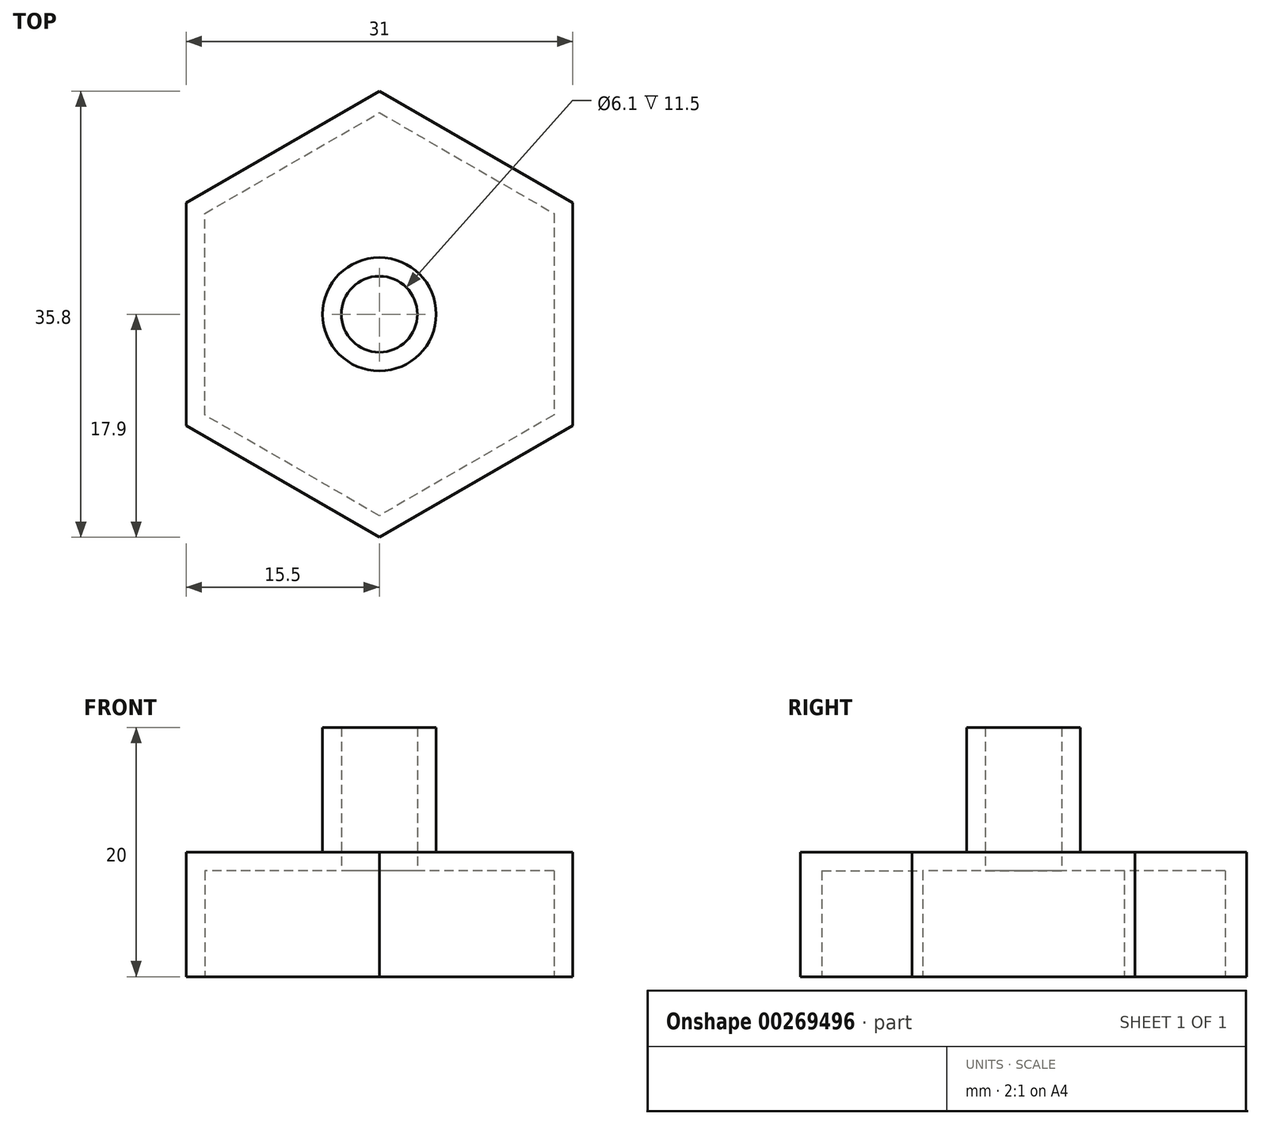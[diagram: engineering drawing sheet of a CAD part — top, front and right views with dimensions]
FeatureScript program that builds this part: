
annotation { "Feature Type Name" : "Feature", "Feature Type Description" : "" }
export const myFeature = defineFeature(function(context is Context, id is Id, definition is map)
    precondition{}
    {
        {
            var Q0;
            Q0=qCreatedBy(makeId("Top.planeOp"),FACE);
            var sketch = newSketch(context, id + "F0", { "sketchPlane" : qUnion([Q0])});
            skCircle(sketch, "E0.cCircle", {"center": v(0, 0) * mm, "radius": 17.9 * mm, "construction": true});
            skLineSegment(sketch, "E0.0", {"start": v(0, -17.9) * mm, "end": v(-15.5, -8.95) * mm});
            skLineSegment(sketch, "E0.1", {"start": v(-15.5, -8.95) * mm, "end": v(-15.5, 8.95) * mm});
            skLineSegment(sketch, "E0.2", {"start": v(-15.5, 8.95) * mm, "end": v(0, 17.9) * mm});
            skLineSegment(sketch, "E0.3", {"start": v(0, 17.9) * mm, "end": v(15.5, 8.95) * mm});
            skLineSegment(sketch, "E0.4", {"start": v(15.5, 8.95) * mm, "end": v(15.5, -8.95) * mm});
            skLineSegment(sketch, "E0.5", {"start": v(15.5, -8.95) * mm, "end": v(0, -17.9) * mm});
            skSolve(sketch);
        }
        {
            var Q0;
            Q0 = qSketchRegion(id + "F0", true);
            extrude(context, id + "F1", {"entities" : qUnion([Q0]), "depth" : 10 * mm});
        }
        {
            var Q0;
            Q0=makeQuery(id+"F1.opExtrude","CAP_FACE",FACE,{"disambiguationData":[OSD([sQuery(id+"F0.wireOp",EDGE,"E0.0"),sQuery(id+"F0.wireOp",EDGE,"E0.1"),sQuery(id+"F0.wireOp",EDGE,"E0.2"),sQuery(id+"F0.wireOp",EDGE,"E0.3"),sQuery(id+"F0.wireOp",EDGE,"E0.4"),sQuery(id+"F0.wireOp",EDGE,"E0.5")])],"isStart":false});
            var sketch = newSketch(context, id + "F2", { "sketchPlane" : qUnion([Q0])});
            skCircle(sketch, "E1", {"center": v(0, 0) * mm, "radius": 4.55 * mm});
            skSolve(sketch);
        }
        {
            var Q0;
            Q0=makeQuery(id+"F2.imprint","IMPRINT",FACE,{"disambiguationData":[TD([[makeQuery(id+"F2.imprint","IMPRINT",EDGE,{"derivedFrom":sQuery(id+"F2.wireOp",EDGE,"E1")}),1.0]])]});
            extrude(context, id + "F3", {"entities" : qUnion([Q0]), "operationType" : NewBodyOperationType.ADD, "endBound" : BoundingType.SYMMETRIC, "depth" : 20 * mm});
        }
        {
            var Q0;
            Q0=makeQuery(id+"F1.opExtrude","CAP_FACE",FACE,{"disambiguationData":[OSD([sQuery(id+"F0.wireOp",EDGE,"E0.0"),sQuery(id+"F0.wireOp",EDGE,"E0.1"),sQuery(id+"F0.wireOp",EDGE,"E0.2"),sQuery(id+"F0.wireOp",EDGE,"E0.3"),sQuery(id+"F0.wireOp",EDGE,"E0.4"),sQuery(id+"F0.wireOp",EDGE,"E0.5")])],"isStart":true});
            var Q1;
            Q1=makeQuery(id+"F3.opExtrude","CAP_FACE",FACE,{"disambiguationData":[OSD([sQuery(id+"F2.wireOp",EDGE,"E1")])],"isStart":false});
            shell(context, id + "F4", {"entities" : qUnion([Q0, Q1]), "thickness" : 1.5 * mm});
        }
    });
